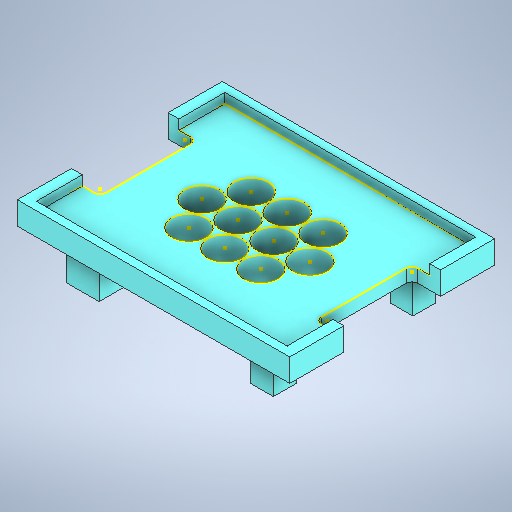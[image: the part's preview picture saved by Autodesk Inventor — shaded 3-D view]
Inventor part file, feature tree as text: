
AUTODESK INVENTOR PART (.ipt)
format: ipt  version: 2025.2 (Build 292293000, 293)  size: 928,256 bytes
history: native  units: mm
features: sketch x9, projected_geometry x9, extrude x8
ambient origin geometry x8: Origin, YZ Plane, XZ Plane, XY Plane, X Axis, Y Axis, Z Axis, Center Point
bodies: Solid1 (feature_tree)
feature tree (26):
  extrude  "Extrusion1"  Depth=21.0mm
  sketch  "Sketch4"  dims[d4=21.0mm d6=21.0mm]
  extrude  "Extrusion7"  Depth=21.0mm
  sketch  "Sketch5"  dims[d8=21.0mm d10=21.0mm]
  extrude  "Extrusion8"  Depth=21.0mm
  extrude  "Extrusion6"  Depth=21.0mm
  extrude  "Extrusion9"  Depth=15.0mm TaperAngle=0.0deg
  extrude  "Extrusion11"  Depth=21.0mm
  extrude  "Extrusion12"  Depth=153.4mm
  extrude  "Extrusion14"  Depth=0.5mm
  sketch  "Sketch14"  dims[d124=7.23mm d125=7.23mm d126=0.0mm d127=0.0mm d140=7.23mm d144=23.0mm d145=23.0mm d146=23.0mm d147=23.0mm d148=23.0mm d149=23.0mm d150=23.0mm d151=23.0mm d152=23.0mm d153=23.0mm d154=25.0mm d155=25.0mm d156=25.0mm d157=25.0mm d158=25.0mm d159=25.0mm d160=25.0mm d161=25.0mm d162=25.0mm d163=25.0mm d164=115.4mm d165=8.0mm d166=0.0mm d169=5.0mm d170=6.646447mm d171=166.692894mm d172=125.4mm d173=6.0mm d174=8.0mm d175=0.0mm d176=0.0mm d177=0.0mm d178=0.0mm d179=31.75mm d180=7.228mm d181=7.228mm d182=31.75mm d183=31.75mm d184=7.228mm d185=7.228mm d186=31.75mm d209=30.0mm d210=20.0mm d211=20.0mm d212=20.0mm d213=15.0mm d214=15.0mm d215=30.0mm d216=20.0mm d217=14.0mm d218=14.0mm d219=25.0mm d220=0.0mm d221=6.646447mm d222=70.0mm d223=0.0mm d224=30.0mm d225=30.0mm d226=20.0mm d227=20.0mm d231=10.0mm d232=0.0mm d234=0.0mm d235=0.0mm d228=0.5mm d229=0.872665mm d230=0.5mm d236=0.872665mm d237=0.5mm d238=0.872665mm]
  sketch  "Sketch1"  dims[d0=21.0mm d2=21.0mm]
  projected_geometry  "Projected Loop1"
  sketch  "Sketch6"  dims[d11=21.0mm d13=21.0mm]
  projected_geometry  "Projected Loop4"
  sketch  "Sketch7"  dims[d14=21.0mm]
  projected_geometry  "Projected Loop5"
  projected_geometry  "Projected Loop6"
  sketch  "Sketch10"  dims[d16=20.0mm d17=20.0mm d18=20.0mm d19=20.0mm d20=20.0mm d21=20.0mm d22=20.0mm d23=20.0mm d24=15.0mm d25=0.0mm]
  projected_geometry  "Projected Loop9"
  sketch  "Sketch11"  dims[d53=21.0mm d91=1.0mm]
  projected_geometry  "Projected Loop10"
  projected_geometry  "Projected Loop11"
  sketch  "Sketch13"  dims[d104=153.4mm d123=7.23mm]
  projected_geometry  "Projected Loop13"
  projected_geometry  "Projected Loop14"
